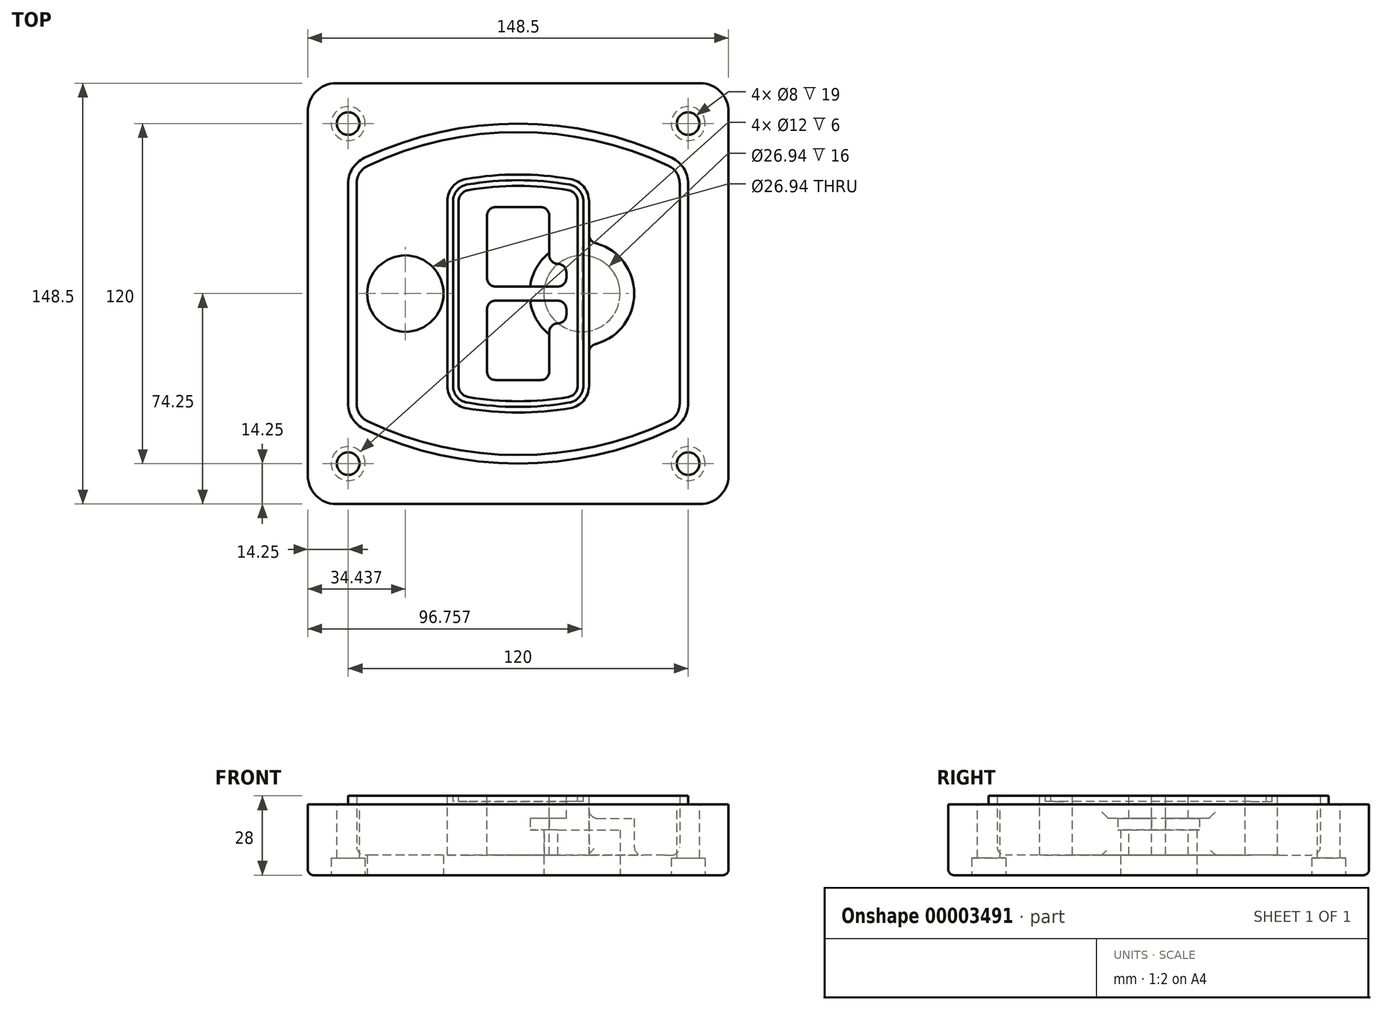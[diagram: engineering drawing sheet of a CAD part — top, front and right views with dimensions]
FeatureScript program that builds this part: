
annotation { "Feature Type Name" : "Feature", "Feature Type Description" : "" }
export const myFeature = defineFeature(function(context is Context, id is Id, definition is map)
    precondition{}
    {
        {
            var Q0;
            Q0=qCreatedBy(makeId("Top.planeOp"),FACE);
            var sketch = newSketch(context, id + "F0", { "sketchPlane" : qUnion([Q0])});
            skPoint(sketch, "E0.rect.middle", {"position": v(0, 0) * mm});
            skLineSegment(sketch, "E1.bottom", {"start": v(-64.25, -74.25) * mm, "end": v(64.25, -74.25) * mm});
            skLineSegment(sketch, "E1.top", {"start": v(-64.25, 74.25) * mm, "end": v(64.25, 74.25) * mm});
            skLineSegment(sketch, "E1.left", {"start": v(-74.25, -64.25) * mm, "end": v(-74.25, 64.25) * mm});
            skLineSegment(sketch, "E1.right", {"start": v(74.25, -64.25) * mm, "end": v(74.25, 64.25) * mm});
            skLineSegment(sketch, "E2", {"start": v(-74.25, 74.25) * mm, "end": v(74.25, -74.25) * mm, "construction": true});
            skLineSegment(sketch, "E3", {"start": v(74.25, 74.25) * mm, "end": v(-74.25, -74.25) * mm, "construction": true});
            skCircle(sketch, "E4", {"center": v(-60, 60) * mm, "radius": 4 * mm});
            skCircle(sketch, "E5", {"center": v(60, 60) * mm, "radius": 4 * mm});
            skCircle(sketch, "E6", {"center": v(60, -60) * mm, "radius": 4 * mm});
            skCircle(sketch, "E7", {"center": v(-60, -60) * mm, "radius": 4 * mm});
            skLineSegment(sketch, "E8", {"start": v(-60, 60) * mm, "end": v(60, 60) * mm, "construction": true});
            skLineSegment(sketch, "E9", {"start": v(60, 60) * mm, "end": v(60, -60) * mm, "construction": true});
            skLineSegment(sketch, "E10", {"start": v(60, -60) * mm, "end": v(-60, -60) * mm, "construction": true});
            skLineSegment(sketch, "E11", {"start": v(-60, -60) * mm, "end": v(-60, 60) * mm, "construction": true});
            skLineSegment(sketch, "E12", {"start": v(-60, 38.83) * mm, "end": v(-60, -38.83) * mm});
            skLineSegment(sketch, "E13", {"start": v(60, 38.83) * mm, "end": v(60, -38.83) * mm});
            skArc(sketch, "E14", {"start": v(54.26, 47.88) * mm, "mid": v(0, 60) * mm, "end": v(-54.26, 47.88) * mm});
            skArc(sketch, "E15", {"start": v(-54.26, -47.88) * mm, "mid": v(0, -60) * mm, "end": v(54.26, -47.88) * mm});
            skLineSegment(sketch, "E16", {"start": v(-60, 0) * mm, "end": v(60, 0) * mm, "construction": true});
            skPoint(sketch, "E17.visualSharp", {"position": v(-60, -45) * mm});
            skArc(sketch, "E17.filletArc", {"start": v(-60, -38.83) * mm, "mid": v(-58.44, -44.2) * mm, "end": v(-54.26, -47.88) * mm});
            skPoint(sketch, "E18.visualSharp", {"position": v(-60, 45) * mm});
            skArc(sketch, "E18.filletArc", {"start": v(-54.26, 47.88) * mm, "mid": v(-58.44, 44.2) * mm, "end": v(-60, 38.83) * mm});
            skPoint(sketch, "E19.visualSharp", {"position": v(60, 45) * mm});
            skArc(sketch, "E19.filletArc", {"start": v(60, 38.83) * mm, "mid": v(58.44, 44.2) * mm, "end": v(54.26, 47.88) * mm});
            skPoint(sketch, "E20.visualSharp", {"position": v(60, -45) * mm});
            skArc(sketch, "E20.filletArc", {"start": v(54.26, -47.88) * mm, "mid": v(58.44, -44.2) * mm, "end": v(60, -38.83) * mm});
            skPoint(sketch, "E21.visualSharp", {"position": v(-74.25, 74.25) * mm});
            skArc(sketch, "E21.filletArc", {"start": v(-64.25, 74.25) * mm, "mid": v(-71.32, 71.32) * mm, "end": v(-74.25, 64.25) * mm});
            skPoint(sketch, "E22.visualSharp", {"position": v(74.25, 74.25) * mm});
            skArc(sketch, "E22.filletArc", {"start": v(74.25, 64.25) * mm, "mid": v(71.32, 71.32) * mm, "end": v(64.25, 74.25) * mm});
            skPoint(sketch, "E23.visualSharp", {"position": v(74.25, -74.25) * mm});
            skArc(sketch, "E23.filletArc", {"start": v(64.25, -74.25) * mm, "mid": v(71.32, -71.32) * mm, "end": v(74.25, -64.25) * mm});
            skPoint(sketch, "E24.visualSharp", {"position": v(-74.25, -74.25) * mm});
            skArc(sketch, "E24.filletArc", {"start": v(-74.25, -64.25) * mm, "mid": v(-71.32, -71.32) * mm, "end": v(-64.25, -74.25) * mm});
            skArc(sketch, "E25.0", {"start": v(57, 38.83) * mm, "mid": v(55.9, 42.58) * mm, "end": v(52.98, 45.17) * mm});
            skLineSegment(sketch, "E25.1", {"start": v(57, 38.83) * mm, "end": v(57, -38.83) * mm});
            skArc(sketch, "E25.2", {"start": v(52.98, -45.17) * mm, "mid": v(55.9, -42.58) * mm, "end": v(57, -38.83) * mm});
            skArc(sketch, "E25.3", {"start": v(-52.98, -45.17) * mm, "mid": v(0, -57) * mm, "end": v(52.98, -45.17) * mm});
            skArc(sketch, "E25.4", {"start": v(-57, -38.83) * mm, "mid": v(-55.9, -42.58) * mm, "end": v(-52.98, -45.17) * mm});
            skArc(sketch, "E25.5", {"start": v(52.98, 45.17) * mm, "mid": v(0, 57) * mm, "end": v(-52.98, 45.17) * mm});
            skLineSegment(sketch, "E25.6", {"start": v(-57, 38.83) * mm, "end": v(-57, -38.83) * mm});
            skArc(sketch, "E25.7", {"start": v(-52.98, 45.17) * mm, "mid": v(-55.9, 42.58) * mm, "end": v(-57, 38.83) * mm});
            skArc(sketch, "E26.0", {"start": v(-55.96, 51.5) * mm, "mid": v(-61.82, 46.33) * mm, "end": v(-64, 38.83) * mm});
            skArc(sketch, "E26.1", {"start": v(55.96, 51.5) * mm, "mid": v(0, 64) * mm, "end": v(-55.96, 51.5) * mm});
            skArc(sketch, "E26.2", {"start": v(64, 38.83) * mm, "mid": v(61.82, 46.33) * mm, "end": v(55.96, 51.5) * mm});
            skLineSegment(sketch, "E26.3", {"start": v(64, 38.83) * mm, "end": v(64, -38.83) * mm});
            skArc(sketch, "E26.4", {"start": v(55.96, -51.5) * mm, "mid": v(61.82, -46.33) * mm, "end": v(64, -38.83) * mm});
            skLineSegment(sketch, "E26.5", {"start": v(-64, 38.83) * mm, "end": v(-64, -38.83) * mm});
            skArc(sketch, "E26.6", {"start": v(-55.96, -51.5) * mm, "mid": v(0, -64) * mm, "end": v(55.96, -51.5) * mm});
            skArc(sketch, "E26.7", {"start": v(-64, -38.83) * mm, "mid": v(-61.82, -46.33) * mm, "end": v(-55.96, -51.5) * mm});
            skSolve(sketch);
        }
        {
            var Q0;
            Q0=makeQuery(id+"F0.imprint","IMPRINT",FACE,{"disambiguationData":[TD([[makeQuery(id+"F0.imprint","IMPRINT",EDGE,{"derivedFrom":sQuery(id+"F0.wireOp",EDGE,"E1.bottom")}),1.0]])]});
            var Q1;
            Q1=makeQuery(id+"F0.imprint","IMPRINT",FACE,{"disambiguationData":[TD([[makeQuery(id+"F0.imprint","IMPRINT",EDGE,{"derivedFrom":sQuery(id+"F0.wireOp",EDGE,"E12")}),1.0]])]});
            var Q2;
            Q2=makeQuery(id+"F0.imprint","IMPRINT",FACE,{"disambiguationData":[TD([[makeQuery(id+"F0.imprint","IMPRINT",EDGE,{"derivedFrom":sQuery(id+"F0.wireOp",EDGE,"E25.0")}),1.0]])]});
            var Q3;
            Q3=makeQuery(id+"F0.imprint","IMPRINT",FACE,{"disambiguationData":[TD([[makeQuery(id+"F0.imprint","IMPRINT",EDGE,{"derivedFrom":sQuery(id+"F0.wireOp",EDGE,"E12")}),-1.0]])]});
            extrude(context, id + "F1", {"entities" : qUnion([Q0, Q1, Q2, Q3]), "oppositeDirection" : true, "depth" : 25 * mm});
        }
        {
            var Q0;
            Q0=makeQuery(id+"F0.imprint","IMPRINT",FACE,{"disambiguationData":[TD([[makeQuery(id+"F0.imprint","IMPRINT",EDGE,{"derivedFrom":sQuery(id+"F0.wireOp",EDGE,"E12")}),1.0]])]});
            extrude(context, id + "F2", {"entities" : qUnion([Q0]), "operationType" : NewBodyOperationType.ADD, "depth" : 3 * mm});
        }
        {
            var Q0;
            Q0=makeQuery(id+"F0.imprint","IMPRINT",FACE,{"disambiguationData":[TD([[makeQuery(id+"F0.imprint","IMPRINT",EDGE,{"derivedFrom":sQuery(id+"F0.wireOp",EDGE,"E25.0")}),1.0]])]});
            extrude(context, id + "F3", {"entities" : qUnion([Q0]), "operationType" : NewBodyOperationType.REMOVE, "oppositeDirection" : true, "depth" : 18 * mm});
        }
        {
            var Q0;
            Q0=makeQuery(id+"F2.opExtrude","CAP_FACE",FACE,{"disambiguationData":[OSD([sQuery(id+"F0.wireOp",EDGE,"E12"),sQuery(id+"F0.wireOp",EDGE,"E13"),sQuery(id+"F0.wireOp",EDGE,"E14"),sQuery(id+"F0.wireOp",EDGE,"E15"),sQuery(id+"F0.wireOp",EDGE,"E17.filletArc"),sQuery(id+"F0.wireOp",EDGE,"E18.filletArc"),sQuery(id+"F0.wireOp",EDGE,"E19.filletArc"),sQuery(id+"F0.wireOp",EDGE,"E20.filletArc"),sQuery(id+"F0.wireOp",EDGE,"E25.0"),sQuery(id+"F0.wireOp",EDGE,"E25.1"),sQuery(id+"F0.wireOp",EDGE,"E25.2"),sQuery(id+"F0.wireOp",EDGE,"E25.3"),sQuery(id+"F0.wireOp",EDGE,"E25.4"),sQuery(id+"F0.wireOp",EDGE,"E25.5"),sQuery(id+"F0.wireOp",EDGE,"E25.6"),sQuery(id+"F0.wireOp",EDGE,"E25.7")])],"isStart":false});
            var sketch = newSketch(context, id + "F4", { "sketchPlane" : qUnion([Q0])});
            skArc(sketch, "E27.0", {"start": v(-18.34, -40.45) * mm, "mid": v(0, -42) * mm, "end": v(18.34, -40.45) * mm});
            skArc(sketch, "E28.0", {"start": v(18.34, 40.45) * mm, "mid": v(0, 42) * mm, "end": v(-18.34, 40.45) * mm});
            skLineSegment(sketch, "E29", {"start": v(-25, 32.57) * mm, "end": v(-25, -32.57) * mm});
            skLineSegment(sketch, "E30", {"start": v(25, 32.57) * mm, "end": v(25, -32.57) * mm});
            skLineSegment(sketch, "E31", {"start": v(-25, 39.1) * mm, "end": v(25, 39.1) * mm, "construction": true});
            skLineSegment(sketch, "E32", {"start": v(-25, -39.1) * mm, "end": v(25, -39.1) * mm, "construction": true});
            skPoint(sketch, "E33.visualSharp", {"position": v(-25, 39.1) * mm});
            skArc(sketch, "E33.filletArc", {"start": v(-18.34, 40.45) * mm, "mid": v(-23.11, 37.73) * mm, "end": v(-25, 32.57) * mm});
            skPoint(sketch, "E34.visualSharp", {"position": v(25, 39.1) * mm});
            skArc(sketch, "E34.filletArc", {"start": v(25, 32.57) * mm, "mid": v(23.11, 37.73) * mm, "end": v(18.34, 40.45) * mm});
            skPoint(sketch, "E35.visualSharp", {"position": v(25, -39.1) * mm});
            skArc(sketch, "E35.filletArc", {"start": v(18.34, -40.45) * mm, "mid": v(23.11, -37.73) * mm, "end": v(25, -32.57) * mm});
            skPoint(sketch, "E36.visualSharp", {"position": v(-25, -39.1) * mm});
            skArc(sketch, "E36.filletArc", {"start": v(-25, -32.57) * mm, "mid": v(-23.11, -37.73) * mm, "end": v(-18.34, -40.45) * mm});
            skArc(sketch, "E37.0", {"start": v(52.98, 45.17) * mm, "mid": v(0, 57) * mm, "end": v(-52.98, 45.17) * mm});
            skArc(sketch, "E37.1", {"start": v(-52.98, 45.17) * mm, "mid": v(-55.9, 42.58) * mm, "end": v(-57, 38.83) * mm});
            skLineSegment(sketch, "E37.2", {"start": v(-57, 38.83) * mm, "end": v(-57, -38.83) * mm});
            skArc(sketch, "E37.3", {"start": v(-57, -38.83) * mm, "mid": v(-55.9, -42.58) * mm, "end": v(-52.98, -45.17) * mm});
            skArc(sketch, "E37.4", {"start": v(-52.98, -45.17) * mm, "mid": v(0, -57) * mm, "end": v(52.98, -45.17) * mm});
            skArc(sketch, "E37.5", {"start": v(52.98, -45.17) * mm, "mid": v(55.9, -42.58) * mm, "end": v(57, -38.83) * mm});
            skLineSegment(sketch, "E37.6", {"start": v(57, 38.83) * mm, "end": v(57, -38.83) * mm});
            skArc(sketch, "E37.7", {"start": v(57, 38.83) * mm, "mid": v(55.9, 42.58) * mm, "end": v(52.98, 45.17) * mm});
            skLineSegment(sketch, "E38.0", {"start": v(23, 32.57) * mm, "end": v(23, -32.57) * mm});
            skArc(sketch, "E38.1", {"start": v(18, -38.48) * mm, "mid": v(21.58, -36.44) * mm, "end": v(23, -32.57) * mm});
            skArc(sketch, "E38.2", {"start": v(-18, -38.48) * mm, "mid": v(0, -40) * mm, "end": v(18, -38.48) * mm});
            skArc(sketch, "E38.3", {"start": v(-23, -32.57) * mm, "mid": v(-21.58, -36.44) * mm, "end": v(-18, -38.48) * mm});
            skLineSegment(sketch, "E38.4", {"start": v(-23, 32.57) * mm, "end": v(-23, -32.57) * mm});
            skArc(sketch, "E38.5", {"start": v(23, 32.57) * mm, "mid": v(21.58, 36.44) * mm, "end": v(18, 38.48) * mm});
            skArc(sketch, "E38.6", {"start": v(-18, 38.48) * mm, "mid": v(-21.58, 36.44) * mm, "end": v(-23, 32.57) * mm});
            skArc(sketch, "E38.7", {"start": v(18, 38.48) * mm, "mid": v(0, 40) * mm, "end": v(-18, 38.48) * mm});
            skArc(sketch, "E39.0", {"start": v(21, 32.57) * mm, "mid": v(20.06, 35.15) * mm, "end": v(17.67, 36.5) * mm});
            skLineSegment(sketch, "E39.1", {"start": v(21, 32.57) * mm, "end": v(21, -32.57) * mm});
            skArc(sketch, "E39.2", {"start": v(17.67, -36.5) * mm, "mid": v(20.06, -35.15) * mm, "end": v(21, -32.57) * mm});
            skArc(sketch, "E39.3", {"start": v(-17.67, -36.5) * mm, "mid": v(0, -38) * mm, "end": v(17.67, -36.5) * mm});
            skArc(sketch, "E39.4", {"start": v(-21, -32.57) * mm, "mid": v(-20.06, -35.15) * mm, "end": v(-17.67, -36.5) * mm});
            skArc(sketch, "E39.5", {"start": v(17.67, 36.5) * mm, "mid": v(0, 38) * mm, "end": v(-17.67, 36.5) * mm});
            skLineSegment(sketch, "E39.6", {"start": v(-21, 32.57) * mm, "end": v(-21, -32.57) * mm});
            skArc(sketch, "E39.7", {"start": v(-17.67, 36.5) * mm, "mid": v(-20.06, 35.15) * mm, "end": v(-21, 32.57) * mm});
            skLineSegment(sketch, "E40", {"start": v(-25, 0) * mm, "end": v(25, 0) * mm, "construction": true});
            skLineSegment(sketch, "E41", {"start": v(-11, 5.5) * mm, "end": v(-11, 27.5) * mm});
            skLineSegment(sketch, "E42", {"start": v(-8, 30.5) * mm, "end": v(8, 30.5) * mm});
            skLineSegment(sketch, "E43", {"start": v(11, 27.5) * mm, "end": v(11, 13.5) * mm});
            skLineSegment(sketch, "E44", {"start": v(14, 10.5) * mm, "end": v(14, 10.5) * mm});
            skLineSegment(sketch, "E45", {"start": v(17, 7.5) * mm, "end": v(17, 5.5) * mm});
            skLineSegment(sketch, "E46", {"start": v(14, 2.5) * mm, "end": v(-8, 2.5) * mm});
            skPoint(sketch, "E47.visualSharp", {"position": v(-11, 30.5) * mm});
            skArc(sketch, "E47.filletArc", {"start": v(-8, 30.5) * mm, "mid": v(-10.12, 29.62) * mm, "end": v(-11, 27.5) * mm});
            skPoint(sketch, "E48.visualSharp", {"position": v(11, 30.5) * mm});
            skArc(sketch, "E48.filletArc", {"start": v(11, 27.5) * mm, "mid": v(10.12, 29.62) * mm, "end": v(8, 30.5) * mm});
            skPoint(sketch, "E49.visualSharp", {"position": v(11, 10.5) * mm});
            skArc(sketch, "E49.filletArc", {"start": v(11, 13.5) * mm, "mid": v(11.88, 11.38) * mm, "end": v(14, 10.5) * mm});
            skPoint(sketch, "E50.visualSharp", {"position": v(17, 10.5) * mm});
            skArc(sketch, "E50.filletArc", {"start": v(17, 7.5) * mm, "mid": v(16.12, 9.62) * mm, "end": v(14, 10.5) * mm});
            skPoint(sketch, "E51.visualSharp", {"position": v(17, 2.5) * mm});
            skArc(sketch, "E51.filletArc", {"start": v(14, 2.5) * mm, "mid": v(16.12, 3.38) * mm, "end": v(17, 5.5) * mm});
            skPoint(sketch, "E52.visualSharp", {"position": v(-11, 2.5) * mm});
            skArc(sketch, "E52.filletArc", {"start": v(-11, 5.5) * mm, "mid": v(-10.12, 3.38) * mm, "end": v(-8, 2.5) * mm});
            skLineSegment(sketch, "E53.0.MirrorCS", {"start": v(14, -2.5) * mm, "end": v(-8, -2.5) * mm});
            skArc(sketch, "E54.0.MirrorCS", {"start": v(-11, -5.5) * mm, "mid": v(-10.12, -3.38) * mm, "end": v(-8, -2.5) * mm});
            skLineSegment(sketch, "E55.0.MirrorCS", {"start": v(-11, -5.5) * mm, "end": v(-11, -27.5) * mm});
            skArc(sketch, "E56.0.MirrorCS", {"start": v(-8, -30.5) * mm, "mid": v(-10.12, -29.62) * mm, "end": v(-11, -27.5) * mm});
            skLineSegment(sketch, "E57.0.MirrorCS", {"start": v(-8, -30.5) * mm, "end": v(8, -30.5) * mm});
            skArc(sketch, "E58.0.MirrorCS", {"start": v(11, -27.5) * mm, "mid": v(10.12, -29.62) * mm, "end": v(8, -30.5) * mm});
            skLineSegment(sketch, "E59.0.MirrorCS", {"start": v(11, -27.5) * mm, "end": v(11, -13.5) * mm});
            skArc(sketch, "E60.0.MirrorCS", {"start": v(11, -13.5) * mm, "mid": v(11.88, -11.38) * mm, "end": v(14, -10.5) * mm});
            skArc(sketch, "E61.0.MirrorCS", {"start": v(17, -7.5) * mm, "mid": v(16.12, -9.62) * mm, "end": v(14, -10.5) * mm});
            skLineSegment(sketch, "E62.0.MirrorCS", {"start": v(17, -7.5) * mm, "end": v(17, -5.5) * mm});
            skArc(sketch, "E63.0.MirrorCS", {"start": v(14, -2.5) * mm, "mid": v(16.12, -3.38) * mm, "end": v(17, -5.5) * mm});
            skSolve(sketch);
        }
        {
            var Q0;
            Q0=makeQuery(id+"F4.imprint","IMPRINT",FACE,{"disambiguationData":[TD([[makeQuery(id+"F4.imprint","IMPRINT",EDGE,{"derivedFrom":sQuery(id+"F4.wireOp",EDGE,"E27.0")}),1.0]])]});
            var Q1;
            Q1=makeQuery(id+"F4.imprint","IMPRINT",FACE,{"disambiguationData":[TD([[makeQuery(id+"F4.imprint","IMPRINT",EDGE,{"derivedFrom":sQuery(id+"F4.wireOp",EDGE,"E38.0")}),-1.0]])]});
            var Q2;
            Q2=makeQuery(id+"F4.imprint","IMPRINT",FACE,{"disambiguationData":[TD([[makeQuery(id+"F4.imprint","IMPRINT",EDGE,{"derivedFrom":sQuery(id+"F4.wireOp",EDGE,"E39.0")}),1.0]])]});
            extrude(context, id + "F5", {"entities" : qUnion([Q0, Q1, Q2]), "operationType" : NewBodyOperationType.ADD, "endBound" : BoundingType.UP_TO_NEXT, "oppositeDirection" : true, "depth" : 25 * mm});
        }
        {
            var Q0;
            Q0=makeQuery(id+"F4.imprint","IMPRINT",FACE,{"disambiguationData":[TD([[makeQuery(id+"F4.imprint","IMPRINT",EDGE,{"derivedFrom":sQuery(id+"F4.wireOp",EDGE,"E38.0")}),-1.0]])]});
            extrude(context, id + "F6", {"entities" : qUnion([Q0]), "operationType" : NewBodyOperationType.REMOVE, "oppositeDirection" : true, "depth" : 2 * mm});
        }
        {
            var Q0;
            Q0=makeQuery(id+"F1.opExtrude","CAP_FACE",FACE,{"disambiguationData":[OSD([sQuery(id+"F0.wireOp",EDGE,"E1.bottom"),sQuery(id+"F0.wireOp",EDGE,"E1.top"),sQuery(id+"F0.wireOp",EDGE,"E1.left"),sQuery(id+"F0.wireOp",EDGE,"E1.right"),sQuery(id+"F0.wireOp",EDGE,"E4"),sQuery(id+"F0.wireOp",EDGE,"E5"),sQuery(id+"F0.wireOp",EDGE,"E6"),sQuery(id+"F0.wireOp",EDGE,"E7"),sQuery(id+"F0.wireOp",EDGE,"E21.filletArc"),sQuery(id+"F0.wireOp",EDGE,"E22.filletArc"),sQuery(id+"F0.wireOp",EDGE,"E23.filletArc"),sQuery(id+"F0.wireOp",EDGE,"E24.filletArc")])],"isStart":false});
            var sketch = newSketch(context, id + "F7", { "sketchPlane" : qUnion([Q0])});
            skCircle(sketch, "E64", {"center": v(22.5, 0) * mm, "radius": 13.47 * mm});
            skCircle(sketch, "E65", {"center": v(-39.81, 0) * mm, "radius": 13.47 * mm});
            skLineSegment(sketch, "E66", {"start": v(74.25, 0) * mm, "end": v(-74.25, 0) * mm});
            skCircle(sketch, "E67", {"center": v(22.5, 0) * mm, "radius": 18.47 * mm});
            skCircle(sketch, "E68", {"center": v(60, -60) * mm, "radius": 6 * mm});
            skCircle(sketch, "E69", {"center": v(-60, -60) * mm, "radius": 6 * mm});
            skCircle(sketch, "E70", {"center": v(-60, 60) * mm, "radius": 6 * mm});
            skCircle(sketch, "E71", {"center": v(60, 60) * mm, "radius": 6 * mm});
            skSolve(sketch);
        }
        {
            var Q0;
            {var subQ1=sQuery(id+"F7.wireOp",EDGE,"E66");var subQ4=sQuery(id+"F7.wireOp",EDGE,"E64");var subQ6=makeQuery(id+"F7.imprint","INTERSECT",VERTEX,{"disambiguationData":[OD(0.0)],"derivedFrom":[subQ4,subQ1]});Q0=makeQuery(id+"F7.imprint","IMPRINT",FACE,{"disambiguationData":[TD([[makeQuery(id+"F7.imprint","IMPRINT",EDGE,{"disambiguationData":[TD([[subQ6,-1.0]])],"derivedFrom":subQ4}),-1.0]])]});}
            var Q1;
            {var subQ0=sQuery(id+"F7.wireOp",EDGE,"E66");var subQ1=sQuery(id+"F7.wireOp",EDGE,"E64");var subQ3=makeQuery(id+"F7.imprint","INTERSECT",VERTEX,{"disambiguationData":[OD(0.0)],"derivedFrom":[subQ1,subQ0]});Q1=makeQuery(id+"F7.imprint","IMPRINT",FACE,{"disambiguationData":[TD([[makeQuery(id+"F7.imprint","IMPRINT",EDGE,{"disambiguationData":[TD([[subQ3,-1.0]])],"derivedFrom":subQ1}),1.0]])]});}
            var Q2;
            {var subQ0=sQuery(id+"F7.wireOp",EDGE,"E66");var subQ1=sQuery(id+"F7.wireOp",EDGE,"E64");var subQ3=makeQuery(id+"F7.imprint","INTERSECT",VERTEX,{"disambiguationData":[OD(0.0)],"derivedFrom":[subQ1,subQ0]});Q2=makeQuery(id+"F7.imprint","IMPRINT",FACE,{"disambiguationData":[TD([[makeQuery(id+"F7.imprint","IMPRINT",EDGE,{"disambiguationData":[TD([[subQ3,1.0]])],"derivedFrom":subQ1}),1.0]])]});}
            var Q3;
            {var subQ1=sQuery(id+"F7.wireOp",EDGE,"E66");var subQ4=sQuery(id+"F7.wireOp",EDGE,"E64");var subQ6=makeQuery(id+"F7.imprint","INTERSECT",VERTEX,{"disambiguationData":[OD(0.0)],"derivedFrom":[subQ4,subQ1]});Q3=makeQuery(id+"F7.imprint","IMPRINT",FACE,{"disambiguationData":[TD([[makeQuery(id+"F7.imprint","IMPRINT",EDGE,{"disambiguationData":[TD([[subQ6,1.0]])],"derivedFrom":subQ4}),-1.0]])]});}
            extrude(context, id + "F8", {"entities" : qUnion([Q0, Q1, Q2, Q3]), "operationType" : NewBodyOperationType.ADD, "oppositeDirection" : true, "depth" : 20 * mm});
        }
        {
            var Q0;
            {var subQ0=sQuery(id+"F7.wireOp",EDGE,"E66");var subQ1=sQuery(id+"F7.wireOp",EDGE,"E64");var subQ3=makeQuery(id+"F7.imprint","INTERSECT",VERTEX,{"disambiguationData":[OD(0.0)],"derivedFrom":[subQ1,subQ0]});Q0=makeQuery(id+"F7.imprint","IMPRINT",FACE,{"disambiguationData":[TD([[makeQuery(id+"F7.imprint","IMPRINT",EDGE,{"disambiguationData":[TD([[subQ3,-1.0]])],"derivedFrom":subQ1}),1.0]])]});}
            var Q1;
            {var subQ0=sQuery(id+"F7.wireOp",EDGE,"E66");var subQ1=sQuery(id+"F7.wireOp",EDGE,"E64");var subQ3=makeQuery(id+"F7.imprint","INTERSECT",VERTEX,{"disambiguationData":[OD(0.0)],"derivedFrom":[subQ1,subQ0]});Q1=makeQuery(id+"F7.imprint","IMPRINT",FACE,{"disambiguationData":[TD([[makeQuery(id+"F7.imprint","IMPRINT",EDGE,{"disambiguationData":[TD([[subQ3,1.0]])],"derivedFrom":subQ1}),1.0]])]});}
            extrude(context, id + "F9", {"entities" : qUnion([Q0, Q1]), "operationType" : NewBodyOperationType.REMOVE, "oppositeDirection" : true, "depth" : 16 * mm});
        }
        {
            var Q0;
            {var subQ0=sQuery(id+"F7.wireOp",EDGE,"E66");var subQ1=sQuery(id+"F7.wireOp",EDGE,"E65");var subQ3=makeQuery(id+"F7.imprint","INTERSECT",VERTEX,{"disambiguationData":[OD(0.0)],"derivedFrom":[subQ1,subQ0]});Q0=makeQuery(id+"F7.imprint","IMPRINT",FACE,{"disambiguationData":[TD([[makeQuery(id+"F7.imprint","IMPRINT",EDGE,{"disambiguationData":[TD([[subQ3,-1.0]])],"derivedFrom":subQ1}),1.0]])]});}
            var Q1;
            {var subQ0=sQuery(id+"F7.wireOp",EDGE,"E66");var subQ1=sQuery(id+"F7.wireOp",EDGE,"E65");var subQ3=makeQuery(id+"F7.imprint","INTERSECT",VERTEX,{"disambiguationData":[OD(0.0)],"derivedFrom":[subQ1,subQ0]});Q1=makeQuery(id+"F7.imprint","IMPRINT",FACE,{"disambiguationData":[TD([[makeQuery(id+"F7.imprint","IMPRINT",EDGE,{"disambiguationData":[TD([[subQ3,1.0]])],"derivedFrom":subQ1}),1.0]])]});}
            extrude(context, id + "F10", {"entities" : qUnion([Q0, Q1]), "operationType" : NewBodyOperationType.REMOVE, "oppositeDirection" : true, "depth" : 25 * mm});
        }
        {
            var Q0;
            Q0=makeQuery(id+"F7.imprint","IMPRINT",FACE,{"disambiguationData":[TD([[makeQuery(id+"F7.imprint","IMPRINT",EDGE,{"derivedFrom":sQuery(id+"F7.wireOp",EDGE,"E68")}),1.0]])]});
            var Q1;
            Q1=makeQuery(id+"F7.imprint","IMPRINT",FACE,{"disambiguationData":[TD([[makeQuery(id+"F7.imprint","IMPRINT",EDGE,{"derivedFrom":makeQuery(id+"F1.opExtrude","CAP_EDGE",EDGE,{"disambiguationData":[OSD([sQuery(id+"F0.wireOp",EDGE,"E5")])],"isStart":false})}),-1.0]])]});
            var Q2;
            Q2=makeQuery(id+"F7.imprint","IMPRINT",FACE,{"disambiguationData":[TD([[makeQuery(id+"F7.imprint","IMPRINT",EDGE,{"derivedFrom":sQuery(id+"F7.wireOp",EDGE,"E69")}),1.0]])]});
            var Q3;
            Q3=makeQuery(id+"F7.imprint","IMPRINT",FACE,{"disambiguationData":[TD([[makeQuery(id+"F7.imprint","IMPRINT",EDGE,{"derivedFrom":makeQuery(id+"F1.opExtrude","CAP_EDGE",EDGE,{"disambiguationData":[OSD([sQuery(id+"F0.wireOp",EDGE,"E4")])],"isStart":false})}),-1.0]])]});
            var Q4;
            Q4=makeQuery(id+"F7.imprint","IMPRINT",FACE,{"disambiguationData":[TD([[makeQuery(id+"F7.imprint","IMPRINT",EDGE,{"derivedFrom":sQuery(id+"F7.wireOp",EDGE,"E70")}),1.0]])]});
            var Q5;
            Q5=makeQuery(id+"F7.imprint","IMPRINT",FACE,{"disambiguationData":[TD([[makeQuery(id+"F7.imprint","IMPRINT",EDGE,{"derivedFrom":makeQuery(id+"F1.opExtrude","CAP_EDGE",EDGE,{"disambiguationData":[OSD([sQuery(id+"F0.wireOp",EDGE,"E7")])],"isStart":false})}),-1.0]])]});
            var Q6;
            Q6=makeQuery(id+"F7.imprint","IMPRINT",FACE,{"disambiguationData":[TD([[makeQuery(id+"F7.imprint","IMPRINT",EDGE,{"derivedFrom":sQuery(id+"F7.wireOp",EDGE,"E71")}),1.0]])]});
            var Q7;
            Q7=makeQuery(id+"F7.imprint","IMPRINT",FACE,{"disambiguationData":[TD([[makeQuery(id+"F7.imprint","IMPRINT",EDGE,{"derivedFrom":makeQuery(id+"F1.opExtrude","CAP_EDGE",EDGE,{"disambiguationData":[OSD([sQuery(id+"F0.wireOp",EDGE,"E6")])],"isStart":false})}),-1.0]])]});
            extrude(context, id + "F11", {"entities" : qUnion([Q0, Q1, Q2, Q3, Q4, Q5, Q6, Q7]), "operationType" : NewBodyOperationType.REMOVE, "oppositeDirection" : true, "depth" : 6 * mm});
        }
        {
            var Q0;
            Q0=makeQuery(id+"F9.boolean.opBoolean","COPY",FACE,{"derivedFrom":makeQuery(id+"F9.opExtrude","CAP_FACE",FACE,{"disambiguationData":[OSD([sQuery(id+"F7.wireOp",EDGE,"E64")])],"isStart":false})});
            var sketch = newSketch(context, id + "F12", { "sketchPlane" : qUnion([Q0])});
            skArc(sketch, "E72.0", {"start": v(11, 14.45) * mm, "mid": v(6.45, 9.13) * mm, "end": v(4.2, 2.5) * mm});
            skArc(sketch, "E72.1", {"start": v(4.2, -2.5) * mm, "mid": v(6.45, -9.13) * mm, "end": v(11, -14.45) * mm});
            skLineSegment(sketch, "E73", {"start": v(4.2, -2.5) * mm, "end": v(14, -2.5) * mm});
            skLineSegment(sketch, "E74.0", {"start": v(14, 2.5) * mm, "end": v(4.2, 2.5) * mm});
            skArc(sketch, "E74.1", {"start": v(14, 2.5) * mm, "mid": v(16.12, 3.38) * mm, "end": v(17, 5.5) * mm});
            skLineSegment(sketch, "E74.2", {"start": v(17, 7.5) * mm, "end": v(17, 5.5) * mm});
            skArc(sketch, "E74.3", {"start": v(17, 7.5) * mm, "mid": v(16.12, 9.62) * mm, "end": v(14, 10.5) * mm});
            skArc(sketch, "E74.4", {"start": v(11, 13.5) * mm, "mid": v(11.88, 11.38) * mm, "end": v(14, 10.5) * mm});
            skLineSegment(sketch, "E74.5", {"start": v(11, 14.45) * mm, "end": v(11, 13.5) * mm});
            skLineSegment(sketch, "E74.7", {"start": v(14, -2.5) * mm, "end": v(4.2, -2.5) * mm});
            skArc(sketch, "E74.8", {"start": v(14, -2.5) * mm, "mid": v(16.12, -3.38) * mm, "end": v(17, -5.5) * mm});
            skLineSegment(sketch, "E74.9", {"start": v(17, -7.5) * mm, "end": v(17, -5.5) * mm});
            skArc(sketch, "E74.10", {"start": v(17, -7.5) * mm, "mid": v(16.12, -9.62) * mm, "end": v(14, -10.5) * mm});
            skArc(sketch, "E74.11", {"start": v(11, -13.5) * mm, "mid": v(11.88, -11.38) * mm, "end": v(14, -10.5) * mm});
            skLineSegment(sketch, "E74.12", {"start": v(11, -14.45) * mm, "end": v(11, -13.5) * mm});
            skPoint(sketch, "E75.orphan", {"position": v(11, -27.5) * mm});
            skPoint(sketch, "E76.orphan", {"position": v(-8, -2.5) * mm});
            skPoint(sketch, "E77.orphan", {"position": v(-8, 2.5) * mm});
            skPoint(sketch, "E78.orphan", {"position": v(11, 27.5) * mm});
            skSolve(sketch);
        }
        {
            var Q0;
            {var subQ7=sQuery(id+"F12.wireOp",EDGE,"E72.0");var subQ14=sQuery(id+"F12.wireOp",EDGE,"E72.1");var subQ16=sQuery(id+"F12.wireOp",EDGE,"E74.1");var subQ18=sQuery(id+"F12.wireOp",EDGE,"E74.8");Q0=qUnion([makeQuery(id+"F12.imprint","IMPRINT",FACE,{"disambiguationData":[TD([[makeQuery(id+"F12.imprint","IMPRINT",EDGE,{"derivedFrom":subQ7}),1.0]])]}),makeQuery(id+"F12.imprint","IMPRINT",FACE,{"disambiguationData":[TD([[makeQuery(id+"F12.imprint","IMPRINT",EDGE,{"derivedFrom":subQ14}),1.0]])]}),makeQuery(id+"F12.imprint","IMPRINT",FACE,{"disambiguationData":[TD([[makeQuery(id+"F12.imprint","IMPRINT",EDGE,{"derivedFrom":subQ16}),1.0]])]}),makeQuery(id+"F12.imprint","IMPRINT",FACE,{"disambiguationData":[TD([[makeQuery(id+"F12.imprint","IMPRINT",EDGE,{"derivedFrom":subQ18}),-1.0]])]})]);}
            var Q1;
            Q1=makeQuery(id+"F5.boolean.opBoolean","SPLIT",FACE,{"disambiguationData":[TD([makeQuery(id+"F5.opExtrude","SWEPT_FACE",FACE,{"disambiguationData":[OSD([sQuery(id+"F4.wireOp",EDGE,"E41")])]})])],"derivedFrom":makeQuery(id+"F3.boolean.opBoolean","COPY",FACE,{"derivedFrom":makeQuery(id+"F3.opExtrude","CAP_FACE",FACE,{"disambiguationData":[OSD([sQuery(id+"F0.wireOp",EDGE,"E25.0"),sQuery(id+"F0.wireOp",EDGE,"E25.1"),sQuery(id+"F0.wireOp",EDGE,"E25.2"),sQuery(id+"F0.wireOp",EDGE,"E25.3"),sQuery(id+"F0.wireOp",EDGE,"E25.4"),sQuery(id+"F0.wireOp",EDGE,"E25.5"),sQuery(id+"F0.wireOp",EDGE,"E25.6"),sQuery(id+"F0.wireOp",EDGE,"E25.7")])],"isStart":false})})});
            extrude(context, id + "F13", {"entities" : qUnion([Q0]), "operationType" : NewBodyOperationType.REMOVE, "endBound" : BoundingType.UP_TO_SURFACE, "endBoundEntityFace" : qUnion([Q1]), "depth" : 25 * mm});
        }
        {
            var Q0;
            Q0=makeQuery(id+"F3.boolean.opBoolean","COPY",EDGE,{"derivedFrom":makeQuery(id+"F3.opExtrude","CAP_EDGE",EDGE,{"disambiguationData":[OSD([sQuery(id+"F0.wireOp",EDGE,"E25.6")])],"isStart":false})});
            var Q1;
            Q1=makeQuery(id+"F8.boolean.opBoolean","INTERSECT",EDGE,{"derivedFrom":[makeQuery(id+"F5.opExtrude","SWEPT_FACE",FACE,{"disambiguationData":[OSD([sQuery(id+"F4.wireOp",EDGE,"E30")])]}),makeQuery(id+"F8.opExtrude","CAP_FACE",FACE,{"disambiguationData":[OSD([sQuery(id+"F7.wireOp",EDGE,"E67")])],"isStart":false})]});
            var Q2;
            Q2=makeQuery(id+"F8.boolean.opBoolean","INTERSECT",EDGE,{"disambiguationData":[OD(1.0)],"derivedFrom":[makeQuery(id+"F5.opExtrude","SWEPT_FACE",FACE,{"disambiguationData":[OSD([sQuery(id+"F4.wireOp",EDGE,"E30")])]}),makeQuery(id+"F8.opExtrude","SWEPT_FACE",FACE,{"disambiguationData":[OSD([sQuery(id+"F7.wireOp",EDGE,"E67")])]})]});
            var Q3;
            {var subQ0=sQuery(id+"F4.wireOp",EDGE,"E30");Q3=makeQuery(id+"F8.boolean.opBoolean","SPLIT",EDGE,{"disambiguationData":[TD([makeQuery(id+"F5.opExtrude","SWEPT_FACE",FACE,{"disambiguationData":[OSD([sQuery(id+"F4.wireOp",EDGE,"E35.filletArc")])]})])],"derivedFrom":makeQuery(id+"F5.opExtrude","CAP_EDGE",EDGE,{"disambiguationData":[OSD([subQ0])],"isStart":false})});}
            var Q4;
            {var subQ0=sQuery(id+"F0.wireOp",EDGE,"E25.7");var subQ1=sQuery(id+"F0.wireOp",EDGE,"E25.1");var subQ2=sQuery(id+"F0.wireOp",EDGE,"E25.6");var subQ3=sQuery(id+"F0.wireOp",EDGE,"E25.5");var subQ4=sQuery(id+"F0.wireOp",EDGE,"E25.4");var subQ5=sQuery(id+"F0.wireOp",EDGE,"E25.0");var subQ6=sQuery(id+"F0.wireOp",EDGE,"E25.2");var subQ7=sQuery(id+"F0.wireOp",EDGE,"E25.3");Q4=makeQuery(id+"F8.boolean.opBoolean","INTERSECT",EDGE,{"derivedFrom":[makeQuery(id+"F5.boolean.opBoolean","SPLIT",FACE,{"disambiguationData":[TD([makeQuery(id+"F2.opExtrude","SWEPT_FACE",FACE,{"disambiguationData":[OSD([subQ5])]})])],"derivedFrom":makeQuery(id+"F3.boolean.opBoolean","COPY",FACE,{"derivedFrom":makeQuery(id+"F3.opExtrude","CAP_FACE",FACE,{"disambiguationData":[OSD([subQ5,subQ1,subQ6,subQ7,subQ4,subQ3,subQ2,subQ0])],"isStart":false})})}),makeQuery(id+"F8.opExtrude","SWEPT_FACE",FACE,{"disambiguationData":[OSD([sQuery(id+"F7.wireOp",EDGE,"E67")])]})]});}
            var Q5;
            Q5=makeQuery(id+"F8.boolean.opBoolean","INTERSECT",EDGE,{"disambiguationData":[OD(0.0)],"derivedFrom":[makeQuery(id+"F5.opExtrude","SWEPT_FACE",FACE,{"disambiguationData":[OSD([sQuery(id+"F4.wireOp",EDGE,"E30")])]}),makeQuery(id+"F8.opExtrude","SWEPT_FACE",FACE,{"disambiguationData":[OSD([sQuery(id+"F7.wireOp",EDGE,"E67")])]})]});
            fillet(context, id + "F14", {"entities" : qUnion([Q0, Q1, Q2, Q3, Q4, Q5]), "radius" : 3 * mm, "tangentPropagation" : true, "allowEdgeOverflow" : false});
        }
        {
            var Q0;
            Q0=makeQuery(id+"F1.opExtrude","CAP_EDGE",EDGE,{"disambiguationData":[OSD([sQuery(id+"F0.wireOp",EDGE,"E1.bottom")])],"isStart":false});
            fillet(context, id + "F15", {"entities" : qUnion([Q0]), "radius" : 2 * mm, "tangentPropagation" : true, "allowEdgeOverflow" : false});
        }
    });
